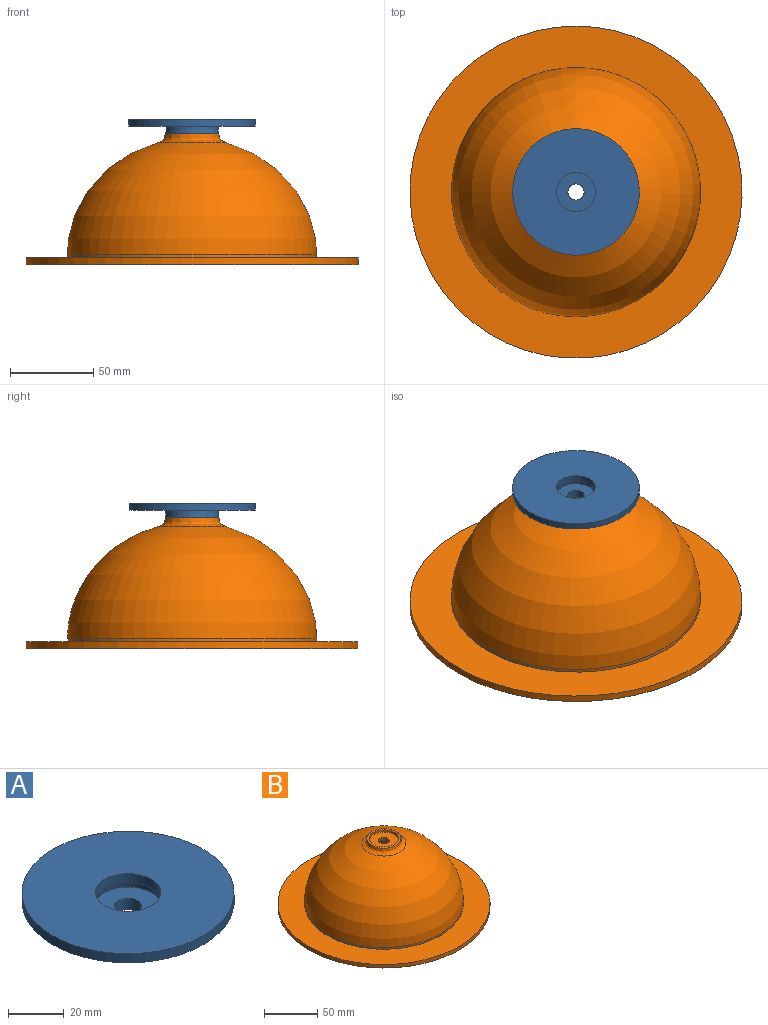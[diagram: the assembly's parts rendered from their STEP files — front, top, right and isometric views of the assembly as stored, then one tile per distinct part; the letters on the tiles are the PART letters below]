
ASSEMBLY  parts=2 mates=1
PART A: 11 faces, bbox 76.2x76.2x11.1 mm
  f0: cone r=11.76mm half-angle=4.5deg, axis (0,0,-1), area 148.3mm2, adj f6,f8
  f1: plane 32.22x32.22mm, normal (0,0,-1), area 201.4mm2, adj f4,f7
  f2: cylinder r=38.1mm len=76.2mm, axis (0,0,-1), area 957.6mm2, adj f3,f5
  f3: plane 76.2x76.2mm, normal (0,0,-1), area 3781.3mm2, adj f2,f4
  f4: cone r=15.75mm half-angle=4.5deg, axis (0,0,-1), area 454.8mm2, adj f1,f3
  f5: plane 76.2x76.2mm, normal (0,0,1), area 4127.7mm2, adj f2,f6
  f6: cylinder r=11.74mm len=23.47mm, axis (0,0,-1), area 295mm2, adj f0,f5
  f7: cylinder r=13.97mm len=27.94mm, axis (0,0,1), area 223mm2, adj f1,f9
  f8: plane 23.78x23.78mm, normal (0,0,1), area 368.7mm2, adj f0,f10
  f9: plane 27.94x27.94mm, normal (0,0,-1), area 537.6mm2, adj f7,f10
  f10: cylinder r=4.9mm len=9.8mm, axis (0,0,1), area 156.5mm2, adj f8,f9
PART B: 14 faces, bbox 208x208x86.9 mm
  f0: offset ~50.64x50.64mm, area 817.7mm2, adj f5,f12
  f1: plane 32.22x32.22mm, normal (0,0,1), area 201.4mm2, adj f2,f10
  f2: bspline ~42.8x42.25mm, area 897.9mm2, adj f1,f3
  f3: revolved ~150x150mm, area 32402.7mm2, adj f2,f4
  f4: cylinder r=75mm len=150mm, axis (0,0,1), area 957.6mm2, adj f3,f8
  f5: revolved ~142x142mm, area 28950.6mm2, adj f0,f6
  f6: cylinder r=71mm len=142mm, axis (0,0,1), area 2690.9mm2, adj f5,f7
  f7: plane 200x200mm, normal (0,0,-1), area 15579.2mm2, adj f6,f9
  f8: plane 200x200mm, normal (0,0,1), area 13744.5mm2, adj f4,f9
  f9: cylinder r=100mm len=200mm, axis (0,0,1), area 2513.3mm2, adj f7,f8
  f10: cylinder r=13.97mm len=27.94mm, axis (0,0,1), area 223mm2, adj f1,f11
  f11: plane 27.94x27.94mm, normal (0,0,1), area 537.6mm2, adj f10,f13
  f12: plane 26.68x26.68mm, normal (0,0,-1), area 483mm2, adj f0,f13
  f13: cylinder r=4.9mm len=9.8mm, axis (0,0,1), area 78.2mm2, adj f11,f12
PLACE A t=(175.88,34.04,17.7)mm
PLACE B t=(175.88,34.04,17.7)mm
MATE fastened B.f13 <-> A.f7  axis (0,0,1) through (175.88,34.04,88.06)mm
